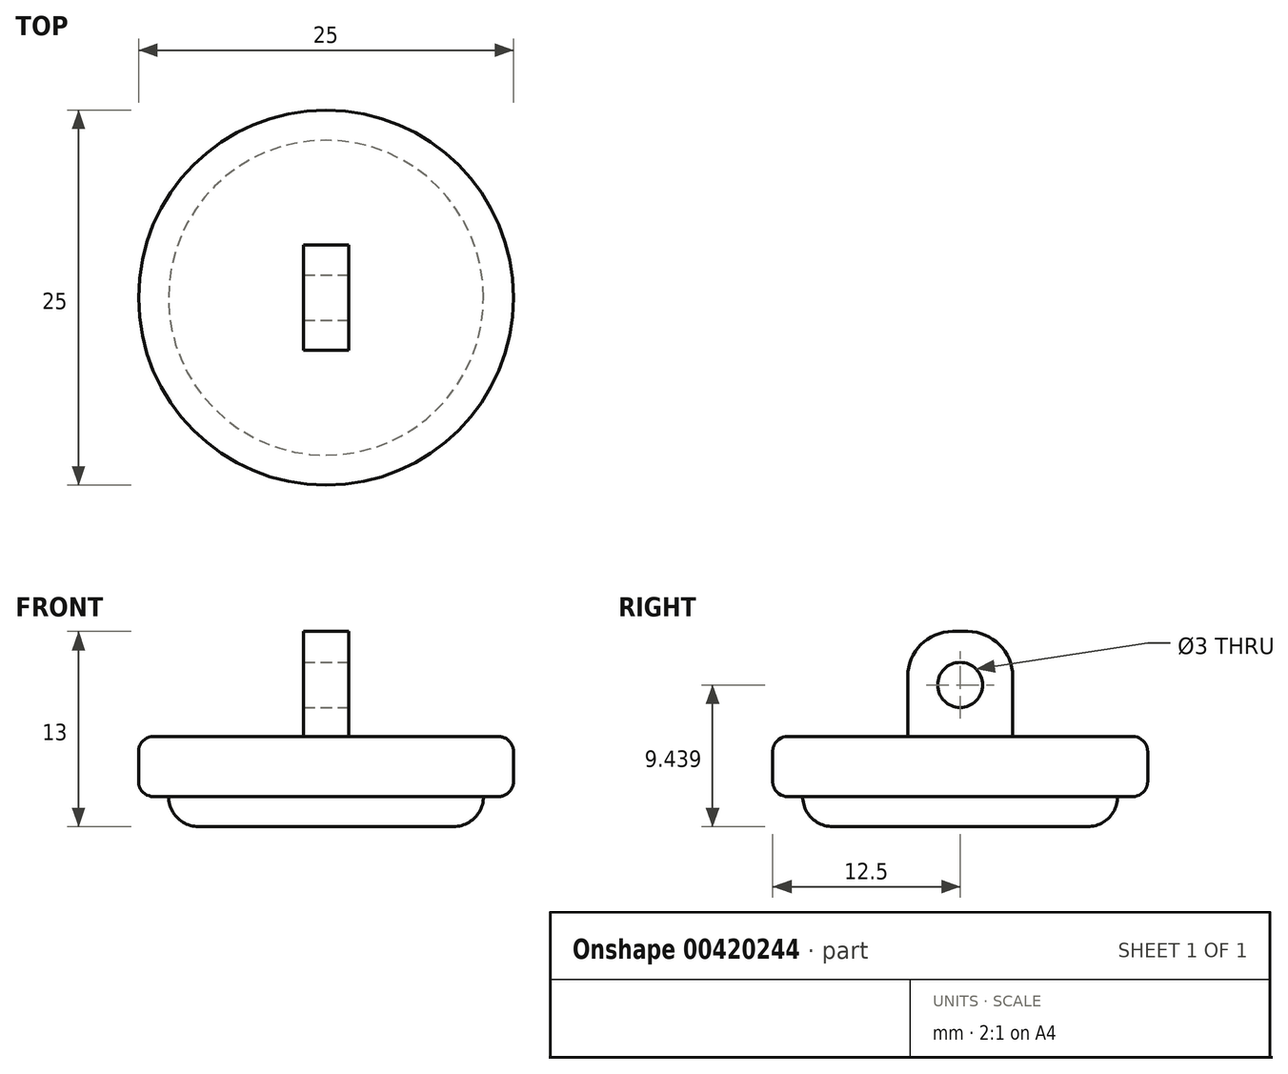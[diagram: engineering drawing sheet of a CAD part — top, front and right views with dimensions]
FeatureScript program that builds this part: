
annotation { "Feature Type Name" : "Feature", "Feature Type Description" : "" }
export const myFeature = defineFeature(function(context is Context, id is Id, definition is map)
    precondition{}
    {
        {
            var Q0;
            Q0=qCreatedBy(makeId("Top.planeOp"),FACE);
            var sketch = newSketch(context, id + "F0", { "sketchPlane" : qUnion([Q0])});
            skCircle(sketch, "E0", {"center": v(0, 0) * mm, "radius": 12.5 * mm});
            skCircle(sketch, "E1", {"center": v(0, 0) * mm, "radius": 10.5 * mm});
            skSolve(sketch);
        }
        {
            var Q0;
            Q0=makeQuery(id+"F0.imprint","IMPRINT",FACE,{"disambiguationData":[TD([[makeQuery(id+"F0.imprint","IMPRINT",EDGE,{"derivedFrom":sQuery(id+"F0.wireOp",EDGE,"E1")}),1.0]])]});
            extrude(context, id + "F1", {"entities" : qUnion([Q0]), "oppositeDirection" : true, "depth" : 2 * mm});
        }
        {
            var Q0;
            Q0=makeQuery(id+"F0.imprint","IMPRINT",FACE,{"disambiguationData":[TD([[makeQuery(id+"F0.imprint","IMPRINT",EDGE,{"derivedFrom":sQuery(id+"F0.wireOp",EDGE,"E1")}),1.0]])]});
            var Q1;
            Q1=makeQuery(id+"F0.imprint","IMPRINT",FACE,{"disambiguationData":[TD([[makeQuery(id+"F0.imprint","IMPRINT",EDGE,{"derivedFrom":sQuery(id+"F0.wireOp",EDGE,"E0")}),1.0]])]});
            extrude(context, id + "F2", {"entities" : qUnion([Q0, Q1]), "operationType" : NewBodyOperationType.ADD, "depth" : 4 * mm});
        }
        {
            var Q0;
            Q0=makeQuery(id+"F2.opExtrude","CAP_FACE",FACE,{"disambiguationData":[OSD([sQuery(id+"F0.wireOp",EDGE,"E0")])],"isStart":false});
            var sketch = newSketch(context, id + "F3", { "sketchPlane" : qUnion([Q0])});
            skLineSegment(sketch, "E2.bottom", {"start": v(1.5, 3.5) * mm, "end": v(-1.5, 3.5) * mm});
            skLineSegment(sketch, "E2.top", {"start": v(1.5, -3.5) * mm, "end": v(-1.5, -3.5) * mm});
            skLineSegment(sketch, "E2.left", {"start": v(1.5, 3.5) * mm, "end": v(1.5, -3.5) * mm});
            skLineSegment(sketch, "E2.right", {"start": v(-1.5, 3.5) * mm, "end": v(-1.5, -3.5) * mm});
            skPoint(sketch, "E2.middle", {"position": v(0, 0) * mm});
            skSolve(sketch);
        }
        {
            var Q0;
            Q0=makeQuery(id+"F3.imprint","IMPRINT",FACE,{"disambiguationData":[TD([[makeQuery(id+"F3.imprint","IMPRINT",EDGE,{"derivedFrom":sQuery(id+"F3.wireOp",EDGE,"E2.bottom")}),1.0]])]});
            extrude(context, id + "F4", {"entities" : qUnion([Q0]), "operationType" : NewBodyOperationType.ADD, "depth" : 7 * mm});
        }
        {
            var Q0;
            Q0=makeQuery(id+"F4.opExtrude","SWEPT_FACE",FACE,{"disambiguationData":[OSD([sQuery(id+"F3.wireOp",EDGE,"E2.left")])]});
            var sketch = newSketch(context, id + "F5", { "sketchPlane" : qUnion([Q0])});
            skCircle(sketch, "E3", {"center": v(0, 7.44) * mm, "radius": 1.5 * mm});
            skSolve(sketch);
        }
        {
            var Q0;
            Q0=makeQuery(id+"F4.opExtrude","CAP_EDGE",EDGE,{"disambiguationData":[OSD([sQuery(id+"F3.wireOp",EDGE,"E2.top")])],"isStart":false});
            var Q1;
            Q1=makeQuery(id+"F4.opExtrude","CAP_EDGE",EDGE,{"disambiguationData":[OSD([sQuery(id+"F3.wireOp",EDGE,"E2.bottom")])],"isStart":false});
            fillet(context, id + "F6", {"entities" : qUnion([Q0, Q1]), "radius" : 3 * mm, "tangentPropagation" : true, "allowEdgeOverflow" : false});
        }
        {
            var Q0;
            Q0=makeQuery(id+"F5.imprint","IMPRINT",FACE,{"disambiguationData":[TD([[makeQuery(id+"F5.imprint","IMPRINT",EDGE,{"derivedFrom":sQuery(id+"F5.wireOp",EDGE,"E3")}),1.0]])]});
            extrude(context, id + "F7", {"entities" : qUnion([Q0]), "operationType" : NewBodyOperationType.REMOVE, "oppositeDirection" : true, "depth" : 25 * mm});
        }
        {
            var Q0;
            Q0=makeQuery(id+"F1.opExtrude","CAP_FACE",FACE,{"disambiguationData":[OSD([sQuery(id+"F0.wireOp",EDGE,"E1")])],"isStart":false});
            fillet(context, id + "F8", {"entities" : qUnion([Q0]), "radius" : 2 * mm, "tangentPropagation" : true, "allowEdgeOverflow" : false});
        }
        {
            var Q0;
            Q0=makeQuery(id+"F2.opExtrude","SWEPT_FACE",FACE,{"disambiguationData":[OSD([sQuery(id+"F0.wireOp",EDGE,"E0")])]});
            fillet(context, id + "F9", {"entities" : qUnion([Q0]), "radius" : 1 * mm, "tangentPropagation" : true, "allowEdgeOverflow" : false});
        }
    });
